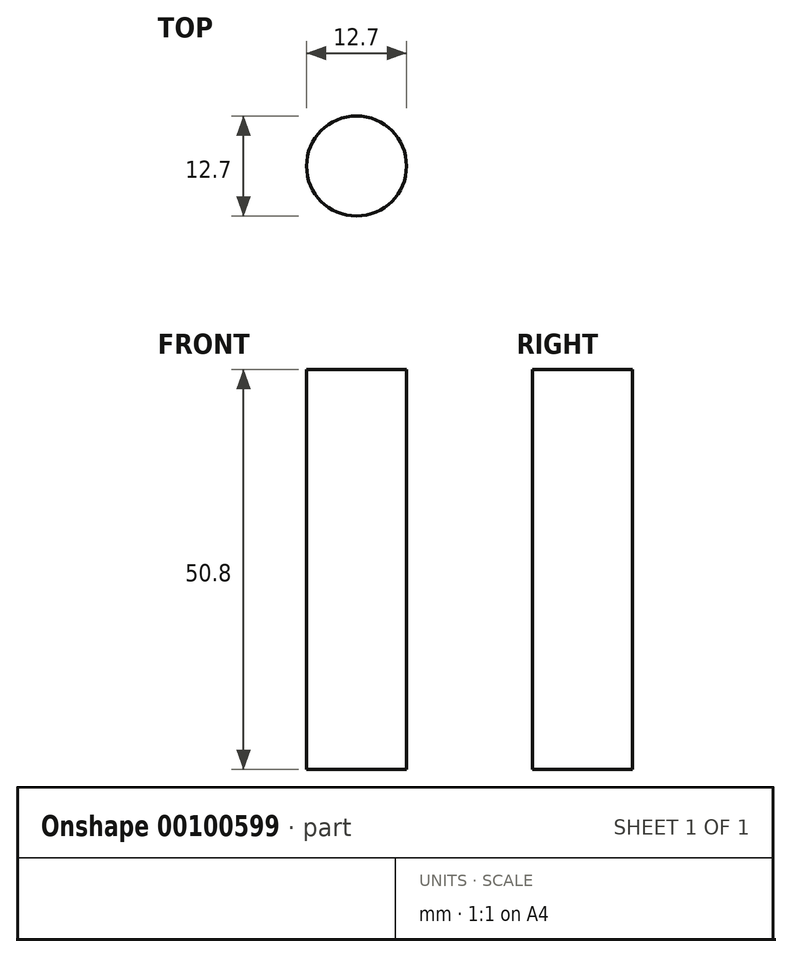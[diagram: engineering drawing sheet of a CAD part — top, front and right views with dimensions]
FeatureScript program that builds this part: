
annotation { "Feature Type Name" : "Feature", "Feature Type Description" : "" }
export const myFeature = defineFeature(function(context is Context, id is Id, definition is map)
    precondition{}
    {
        {
            var Q0;
            Q0=qCreatedBy(makeId("Top.planeOp"),FACE);
            var sketch = newSketch(context, id + "F0", { "sketchPlane" : qUnion([Q0])});
            skCircle(sketch, "E0", {"center": v(0, 0) * mm, "radius": 6.35 * mm});
            skSolve(sketch);
        }
        {
            var Q0;
            Q0 = qSketchRegion(id + "F0", true);
            extrude(context, id + "F1", {"entities" : qUnion([Q0]), "depth" : 50.8 * mm});
        }
    });
